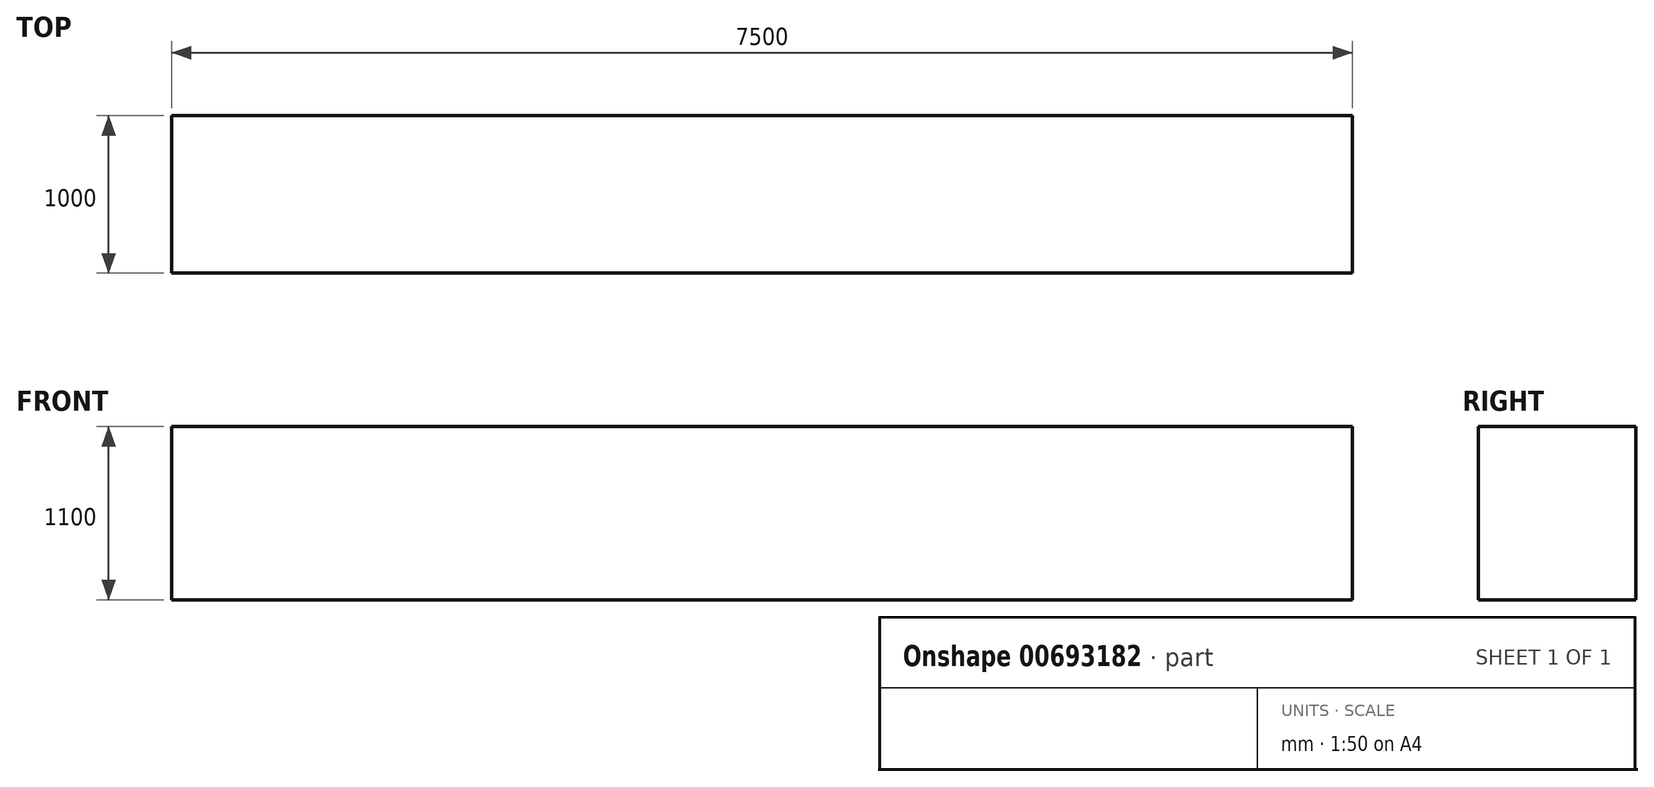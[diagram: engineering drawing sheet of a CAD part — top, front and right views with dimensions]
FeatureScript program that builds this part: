
annotation { "Feature Type Name" : "Feature", "Feature Type Description" : "" }
export const myFeature = defineFeature(function(context is Context, id is Id, definition is map)
    precondition{}
    {
        {
            var Q0;
            Q0=qCreatedBy(makeId("Top.planeOp"),FACE);
            var sketch = newSketch(context, id + "F0", { "sketchPlane" : qUnion([Q0])});
            skLineSegment(sketch, "E0.bottom", {"start": v(-3746.9, -1237.07) * mm, "end": v(3753.1, -1237.07) * mm});
            skLineSegment(sketch, "E0.top", {"start": v(-3746.9, -2237.07) * mm, "end": v(3753.1, -2237.07) * mm});
            skLineSegment(sketch, "E0.left", {"start": v(-3746.9, -1237.07) * mm, "end": v(-3746.9, -2237.07) * mm});
            skLineSegment(sketch, "E0.right", {"start": v(3753.1, -1237.07) * mm, "end": v(3753.1, -2237.07) * mm});
            skSolve(sketch);
        }
        {
            var Q0;
            Q0 = qSketchRegion(id + "F0", true);
            extrude(context, id + "F1", {"entities" : qUnion([Q0]), "depth" : 1100 * mm, "offsetDistance" : 25 * mm});
        }
    });
